# Revit family: Faucet_Mixing-Deck_Mounted-American_Standard-Xavier-9449.301_Series
name_source: partatom
category: Plumbing Fixtures
revit_build: Autodesk Revit 2018 (Build: 20170223_1515(x64)
units: mm (PartAtom-declared; Revit-internal decimal feet)

## family parameters
Always vertical = No
Cut with Voids When Loaded = No
OmniClass Number = 23.45.55.14
OmniClass Title = Single Faucets
Part Type = Normal
Room Calculation Point = No
Round Connector Dimension = Use Diameter
Shared = Yes
Work Plane-Based = Yes

## types (2) — shared parameters
ADA Compliant = Yes
Assembly Code = D2020300
CEC Compliant = Yes
CW Connection = No
CWFU = 1.5
Default Elevation = 0"
Description = Xavier™ Pull-Down Kitchen Faucet with SelectFlo™
Escutcheon Plate = Yes
Flow Rate = 1.8 gpm (6.8 L/min.)
HW Connection = No
HWFU = 1.5
Height = 16 13/16"
IAPMO Compliance = Product meet or exceeds ANSI A117.1, ASME A112.18.1, NSF61/Section 9 & Annex G, CSA B125
Installation Type = Deck Mounted
Length = 10 1/16"
Manufacturer = American Standard
Price = Prices may vary. Please consult Manufacturer Representative for most up-to-date price list.
Product Documentation Link = https://www.americanstandard.ca
Product Page URL = https://www.americanstandard.ca
Revised Date = 09/22/2021
Tempered Connection = Yes
Tempered Water Connection Diameter = 3/8"
Tempered Water Connection Radius = 3/16"
URL = https://www.americanstandard.ca
Vent Connection = No
WFU = 2
Warranty Information = Limited Lifetime Warranty
Waste Connection = No
Width = 2 1/2"

## per-type parameters (varying)
| type | Finish | Material |
| 9449.301.002 | Metal-American Standard-002-Polished Chrome | Metal-American_Standard-002-Polished_Chrome |
| 9449.301.075 | Metal-American Standard-075-Menard's Brushed Nickel | Metal-American Standard-075-Menard's Brushed Nickel |

note: column(s) folded — value = type name in every type: Model

## geometry (parser evidence)
native form markers: Sweep x2
no freeform markers — native parametric forms only
